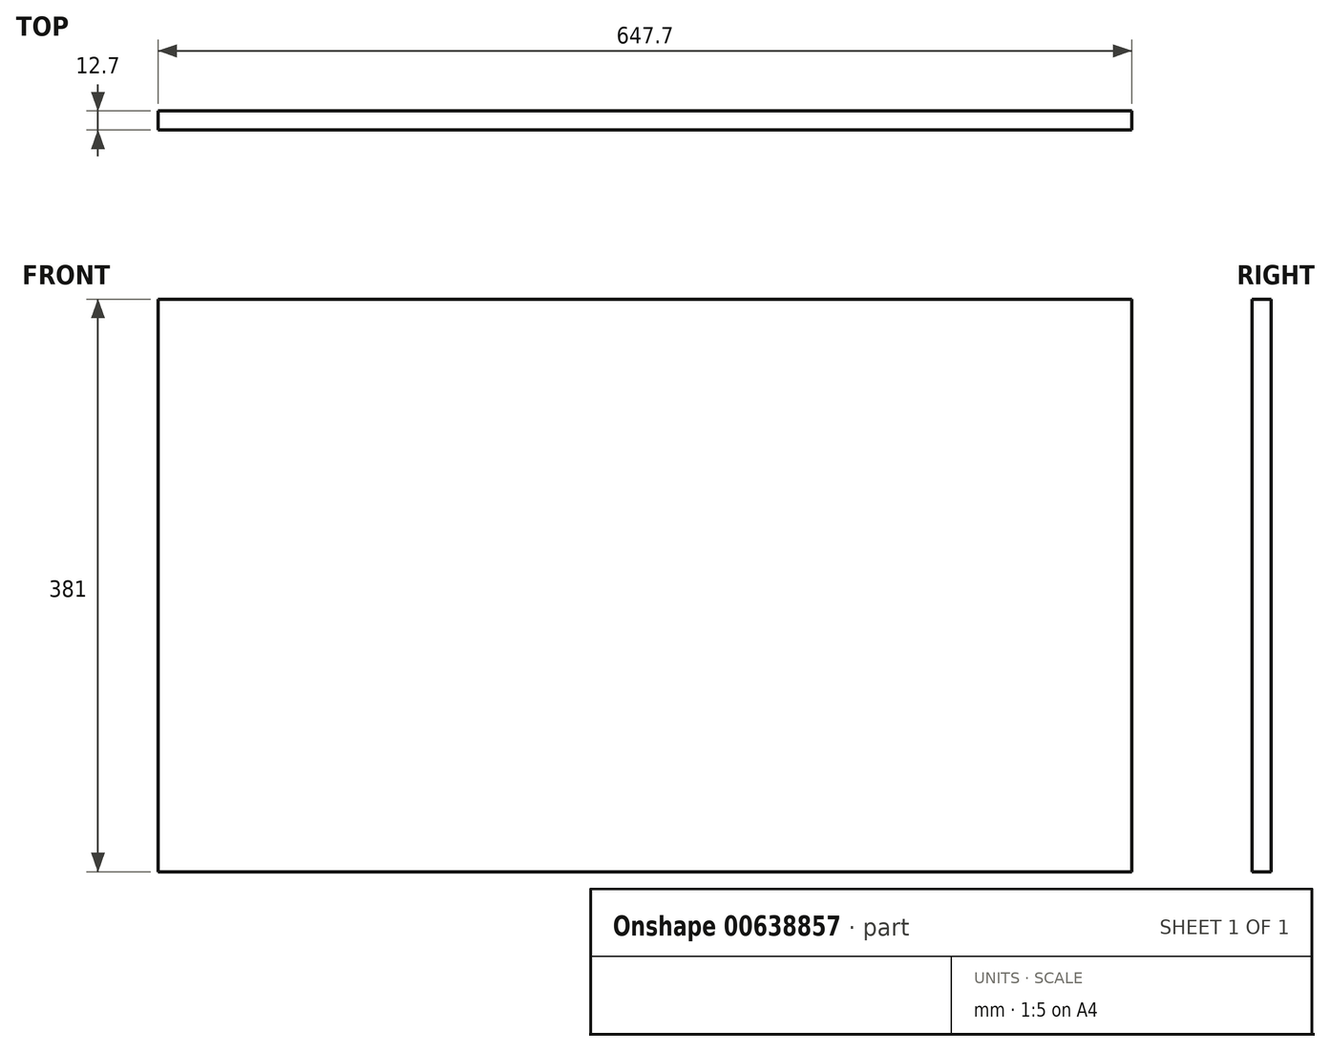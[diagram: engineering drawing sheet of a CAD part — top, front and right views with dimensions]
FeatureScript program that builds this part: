
annotation { "Feature Type Name" : "Feature", "Feature Type Description" : "" }
export const myFeature = defineFeature(function(context is Context, id is Id, definition is map)
    precondition{}
    {
        {
            var Q0;
            Q0=qCreatedBy(makeId("Front.planeOp"),FACE);
            var sketch = newSketch(context, id + "F0", { "sketchPlane" : qUnion([Q0])});
            skLineSegment(sketch, "E0.bottom", {"start": v(323.85, 190.5) * mm, "end": v(-323.85, 190.5) * mm});
            skLineSegment(sketch, "E0.top", {"start": v(323.85, -190.5) * mm, "end": v(-323.85, -190.5) * mm});
            skLineSegment(sketch, "E0.left", {"start": v(323.85, 190.5) * mm, "end": v(323.85, -190.5) * mm});
            skLineSegment(sketch, "E0.right", {"start": v(-323.85, 190.5) * mm, "end": v(-323.85, -190.5) * mm});
            skPoint(sketch, "E0.middle", {"position": v(0, 0) * mm});
            skSolve(sketch);
        }
        {
            var Q0;
            Q0=makeQuery(id+"F0.imprint","IMPRINT",FACE,{"disambiguationData":[TD([[makeQuery(id+"F0.imprint","IMPRINT",EDGE,{"derivedFrom":sQuery(id+"F0.wireOp",EDGE,"E0.bottom")}),1.0]])]});
            extrude(context, id + "F1", {"entities" : qUnion([Q0]), "depth" : 12.7 * mm, "offsetDistance" : 25.4 * mm});
        }
    });
